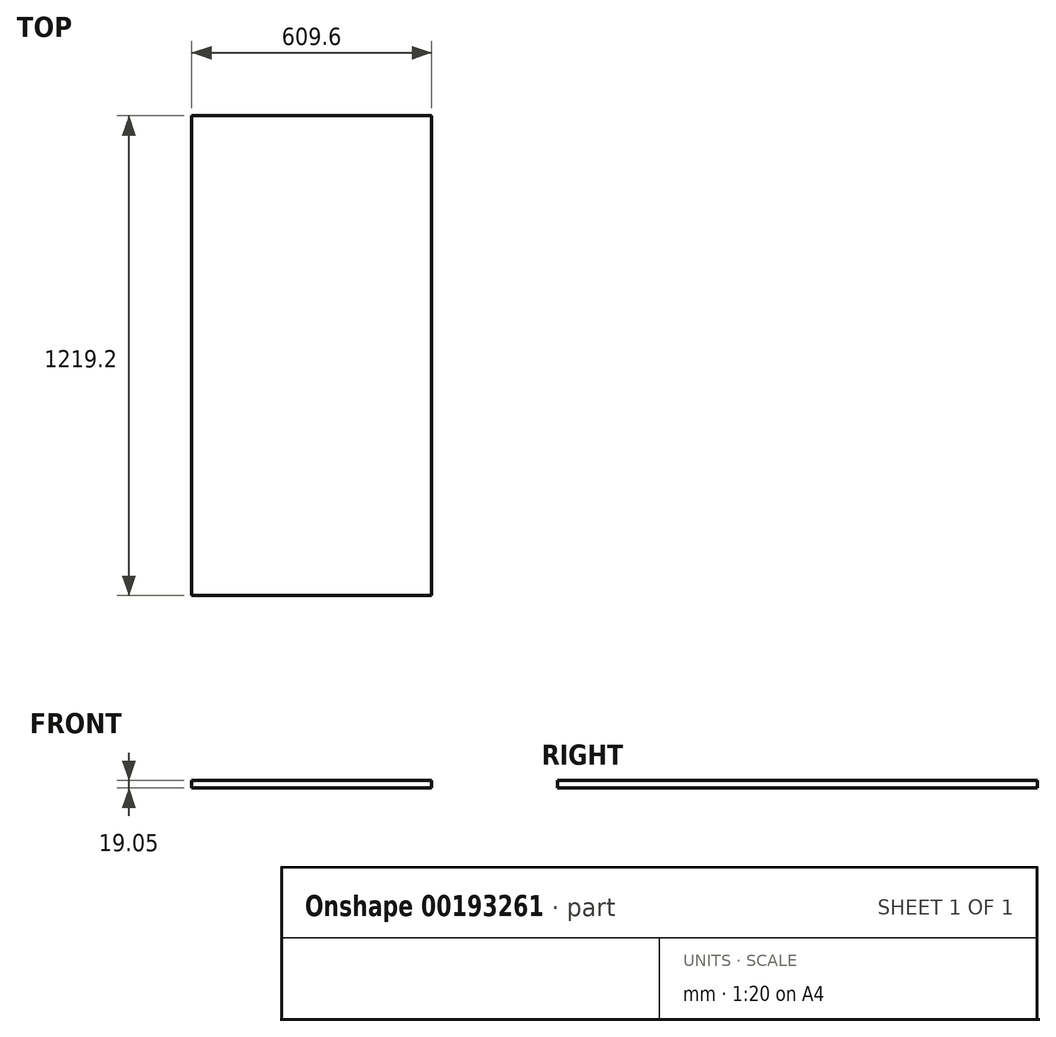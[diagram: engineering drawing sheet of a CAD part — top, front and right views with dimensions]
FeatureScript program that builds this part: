
annotation { "Feature Type Name" : "Feature", "Feature Type Description" : "" }
export const myFeature = defineFeature(function(context is Context, id is Id, definition is map)
    precondition{}
    {
        {
            var Q0;
            Q0=qCreatedBy(makeId("Top.planeOp"),FACE);
            var sketch = newSketch(context, id + "F0", { "sketchPlane" : qUnion([Q0])});
            skLineSegment(sketch, "E0.bottom", {"start": v(304.8, 609.6) * mm, "end": v(-304.8, 609.6) * mm});
            skLineSegment(sketch, "E0.top", {"start": v(304.8, -609.6) * mm, "end": v(-304.8, -609.6) * mm});
            skLineSegment(sketch, "E0.left", {"start": v(304.8, 609.6) * mm, "end": v(304.8, -609.6) * mm});
            skLineSegment(sketch, "E0.right", {"start": v(-304.8, 609.6) * mm, "end": v(-304.8, -609.6) * mm});
            skPoint(sketch, "E0.middle", {"position": v(0, 0) * mm});
            skSolve(sketch);
        }
        {
            var Q0;
            Q0 = qSketchRegion(id + "F0", true);
            extrude(context, id + "F1", {"entities" : qUnion([Q0]), "depth" : (25.4 * .75) * mm});
        }
    });
